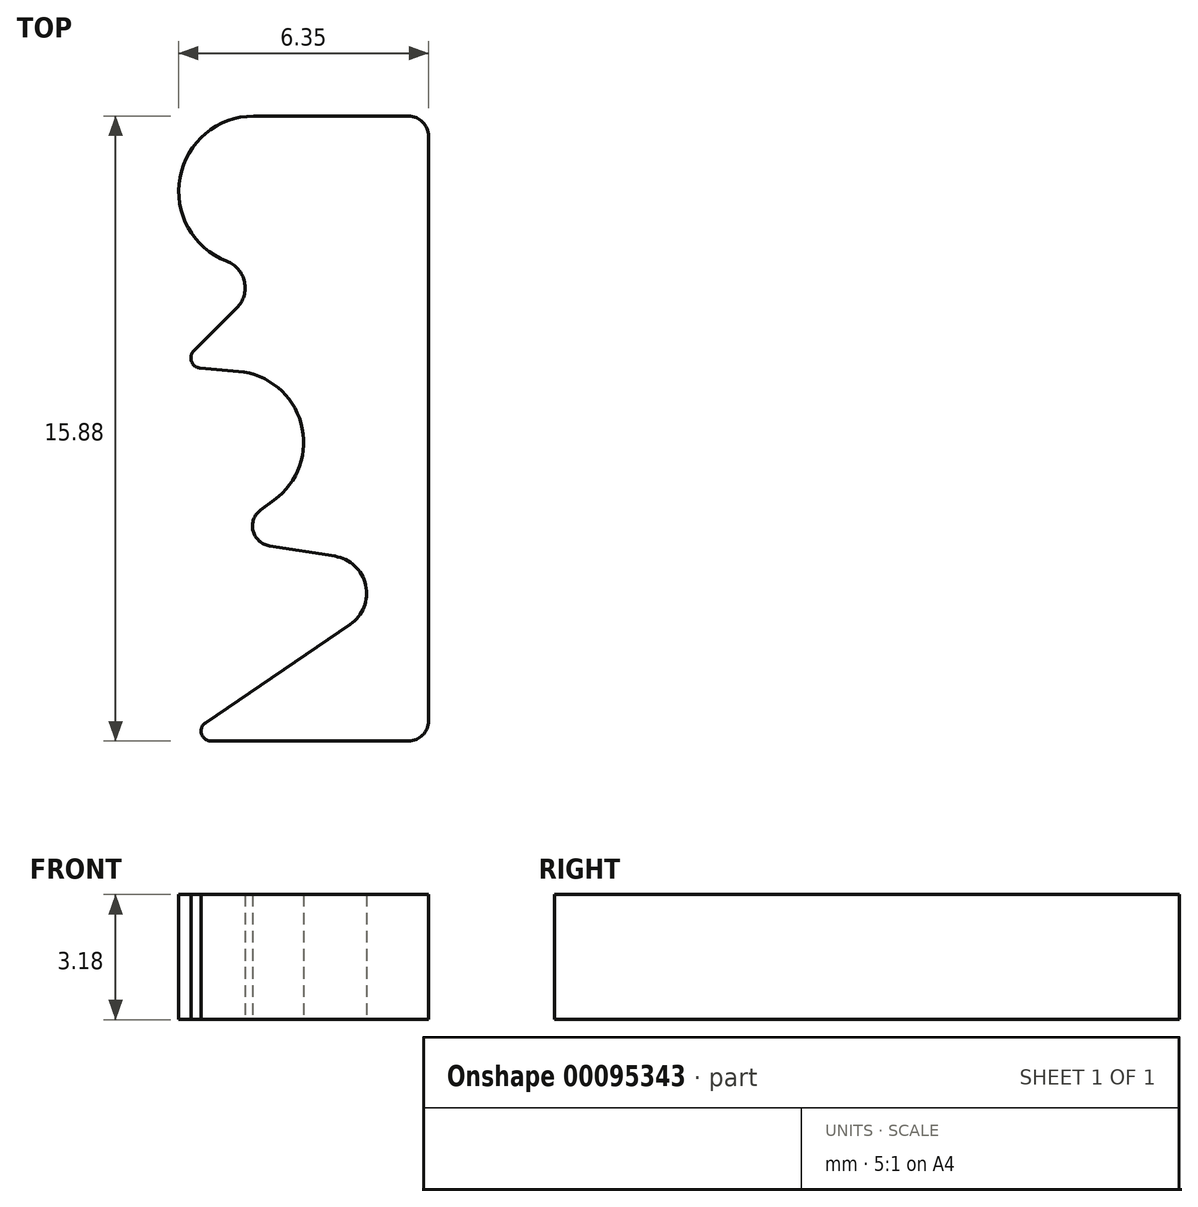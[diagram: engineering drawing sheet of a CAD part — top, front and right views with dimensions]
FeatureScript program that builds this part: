
annotation { "Feature Type Name" : "Feature", "Feature Type Description" : "" }
export const myFeature = defineFeature(function(context is Context, id is Id, definition is map)
    precondition{}
    {
        {
            var Q0;
            Q0=qCreatedBy(makeId("Top.planeOp"),FACE);
            var sketch = newSketch(context, id + "F0", { "sketchPlane" : qUnion([Q0])});
            skLineSegment(sketch, "E0.bottom", {"start": v(-0.5, 0) * mm, "end": v(-5.52, 0) * mm});
            skLineSegment(sketch, "E0.top", {"start": v(-0.5, 15.88) * mm, "end": v(-4.45, 15.88) * mm});
            skLineSegment(sketch, "E0.left", {"start": v(0, 0.5) * mm, "end": v(0, 15.37) * mm});
            skLineSegment(sketch, "E0.right", {"start": v(-6.35, 0) * mm, "end": v(-6.35, 15.88) * mm, "construction": true});
            skLineSegment(sketch, "E1", {"start": v(-6.35, 15.88) * mm, "end": v(0, 0) * mm, "construction": true});
            skLineSegment(sketch, "E2", {"start": v(-0.15, 15.73) * mm, "end": v(-4.54, 11.34) * mm, "construction": true});
            skLineSegment(sketch, "E3", {"start": v(-5.8, 9.48) * mm, "end": v(-4.83, 9.4) * mm});
            skLineSegment(sketch, "E4", {"start": v(-3.92, 6.12) * mm, "end": v(-4.26, 5.87) * mm});
            skLineSegment(sketch, "E5", {"start": v(-4.04, 4.96) * mm, "end": v(-2.38, 4.7) * mm});
            skLineSegment(sketch, "E6", {"start": v(-2, 2.96) * mm, "end": v(-5.67, 0.46) * mm});
            skArc(sketch, "E7", {"start": v(-4.45, 15.88) * mm, "mid": v(-6.32, 14.32) * mm, "end": v(-5.13, 12.2) * mm});
            skArc(sketch, "E8", {"start": v(-4.87, 11) * mm, "mid": v(-4.68, 11.66) * mm, "end": v(-5.13, 12.2) * mm});
            skPoint(sketch, "E9.visualSharp", {"position": v(-6.35, 9.52) * mm});
            skArc(sketch, "E9.filletArc", {"start": v(-5.96, 9.91) * mm, "mid": v(-6.02, 9.64) * mm, "end": v(-5.8, 9.48) * mm});
            skPoint(sketch, "E10.visualSharp", {"position": v(0, 8.97) * mm});
            skArc(sketch, "E10.filletArc", {"start": v(-3.92, 6.12) * mm, "mid": v(-3.24, 8.07) * mm, "end": v(-4.83, 9.4) * mm});
            skArc(sketch, "E11.filletArc", {"start": v(-4.26, 5.87) * mm, "mid": v(-4.46, 5.34) * mm, "end": v(-4.04, 4.96) * mm});
            skPoint(sketch, "E12.visualSharp", {"position": v(0, 4.32) * mm});
            skArc(sketch, "E12.filletArc", {"start": v(-2, 2.96) * mm, "mid": v(-1.6, 3.96) * mm, "end": v(-2.38, 4.7) * mm});
            skPoint(sketch, "E13.visualSharp", {"position": v(-6.35, 0) * mm});
            skArc(sketch, "E13.filletArc", {"start": v(-5.67, 0.46) * mm, "mid": v(-5.77, 0.18) * mm, "end": v(-5.52, 0) * mm});
            skPoint(sketch, "E14.visualSharp", {"position": v(0, 0) * mm});
            skArc(sketch, "E14.filletArc", {"start": v(-0.5, 0) * mm, "mid": v(-0.15, 0.15) * mm, "end": v(0, 0.5) * mm});
            skPoint(sketch, "E15.visualSharp", {"position": v(0, 15.88) * mm});
            skArc(sketch, "E15.filletArc", {"start": v(0, 15.37) * mm, "mid": v(-0.15, 15.73) * mm, "end": v(-0.5, 15.88) * mm});
            skLineSegment(sketch, "E16.trimOffspring", {"start": v(-4.87, 11) * mm, "end": v(-5.96, 9.91) * mm});
            skSolve(sketch);
        }
        {
            var Q0;
            Q0=makeQuery(id+"F0.imprint","IMPRINT",FACE,{"disambiguationData":[TD([[makeQuery(id+"F0.imprint","IMPRINT",EDGE,{"derivedFrom":sQuery(id+"F0.wireOp",EDGE,"E0.bottom")}),-1.0]])]});
            extrude(context, id + "F1", {"entities" : qUnion([Q0]), "endBound" : BoundingType.SYMMETRIC, "depth" : 3.17 * mm});
        }
    });
